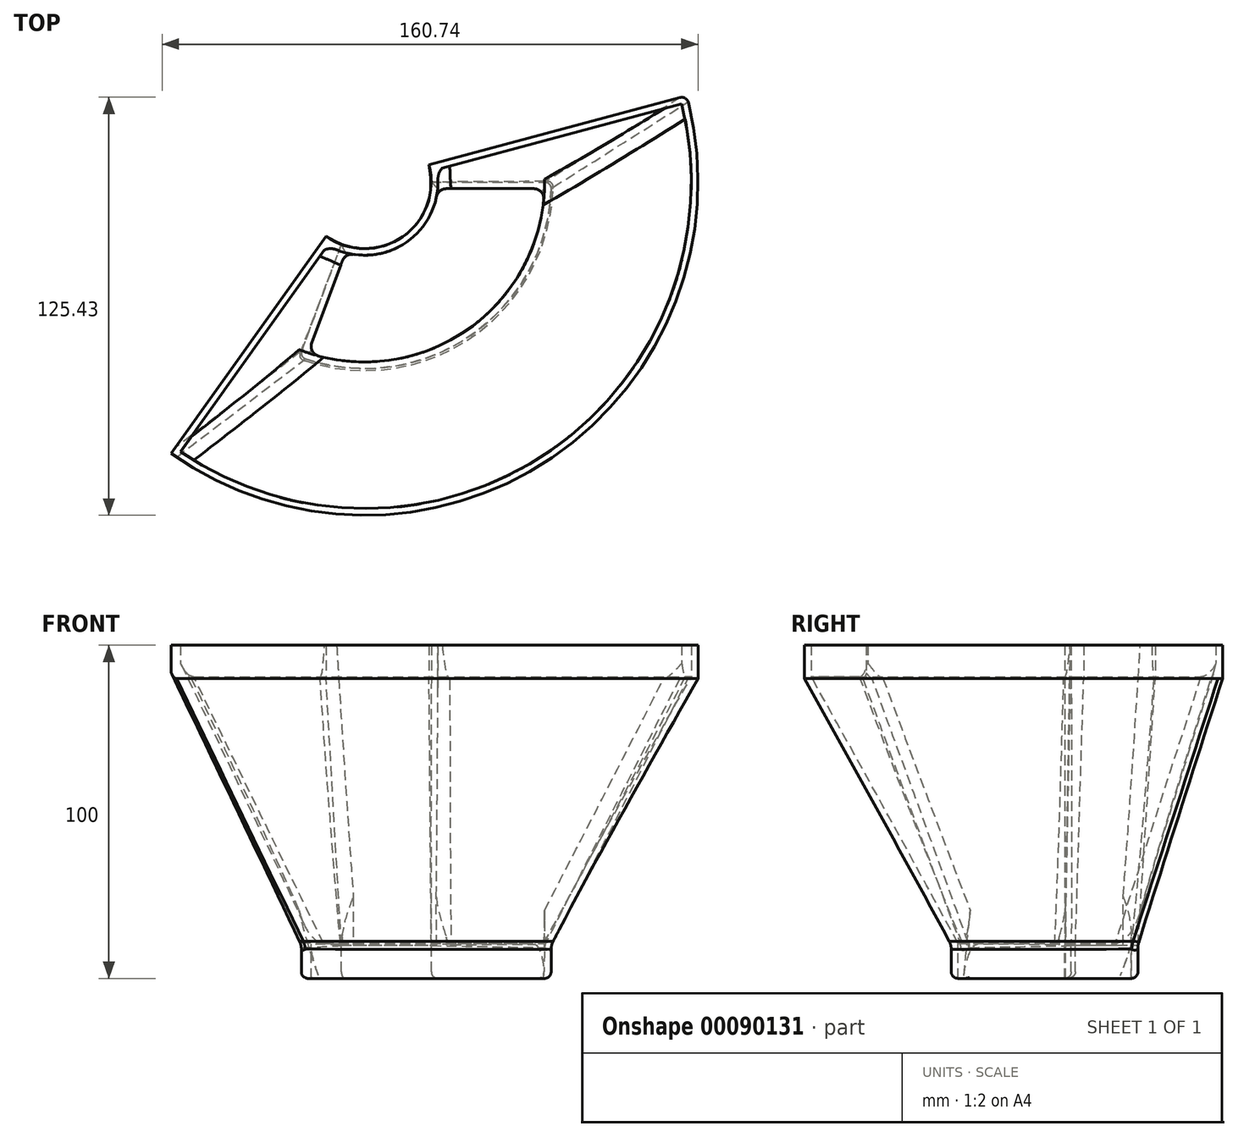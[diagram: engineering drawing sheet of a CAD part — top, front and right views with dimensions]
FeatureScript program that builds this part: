
annotation { "Feature Type Name" : "Feature", "Feature Type Description" : "" }
export const myFeature = defineFeature(function(context is Context, id is Id, definition is map)
    precondition{}
    {
        {
            var Q0;
            Q0=qCreatedBy(makeId("Top.planeOp"),FACE);
            var sketch = newSketch(context, id + "F0", { "sketchPlane" : qUnion([Q0])});
            skArc(sketch, "E0", {"start": v(-6.99, -18.74) * mm, "mid": v(11.4, -16.43) * mm, "end": v(20, 0) * mm});
            skArc(sketch, "E1", {"start": v(56, 0) * mm, "mid": v(31.94, -46) * mm, "end": v(-19.57, -52.47) * mm});
            skLineSegment(sketch, "E2", {"start": v(-6.99, -18.74) * mm, "end": v(-19.57, -52.47) * mm});
            skLineSegment(sketch, "E3", {"start": v(-19.57, -52.47) * mm, "end": v(56, 0) * mm, "construction": true});
            skLineSegment(sketch, "E4", {"start": v(20, 0) * mm, "end": v(56, 0) * mm});
            skLineSegment(sketch, "E5", {"start": v(-19.57, -52.47) * mm, "end": v(0, 0) * mm, "construction": true});
            skLineSegment(sketch, "E6", {"start": v(0, 0) * mm, "end": v(56, 0) * mm, "construction": true});
            skSolve(sketch);
        }
        {
            var Q0;
            Q0=makeQuery(id+"F0.imprint","IMPRINT",FACE,{"disambiguationData":[TD([[makeQuery(id+"F0.imprint","IMPRINT",EDGE,{"derivedFrom":sQuery(id+"F0.wireOp",EDGE,"E0")}),-1.0]])]});
            cPlane(context, id + "F1", {"entities" : qUnion([Q0]), "cplaneType" : CPlaneType.OFFSET, "offset" : 80 * mm, "width" : 150 * mm, "height" : 150 * mm});
        }
        {
            var Q0;
            Q0=makeQuery(id+"F0.imprint","IMPRINT",FACE,{"disambiguationData":[TD([[makeQuery(id+"F0.imprint","IMPRINT",EDGE,{"derivedFrom":sQuery(id+"F0.wireOp",EDGE,"E0")}),-1.0]])]});
            extrude(context, id + "F2", {"entities" : qUnion([Q0]), "oppositeDirection" : true, "depth" : 10 * mm, "hasDraft" : true, "draftAngle" : 0 * degree});
        }
        {
            var Q0;
            Q0=qCreatedBy(id+"F1.planeOp",FACE);
            var sketch = newSketch(context, id + "F3", { "sketchPlane" : qUnion([Q0])});
            skArc(sketch, "E7", {"start": v(57.03, -82.14) * mm, "mid": v(93.9, -34.39) * mm, "end": v(96.6, 25.88) * mm});
            skArc(sketch, "E8", {"start": v(19.32, 5.18) * mm, "mid": v(11.4, -16.43) * mm, "end": v(-11.6, -16.3) * mm});
            skPoint(sketch, "E9.0", {"position": v(31.94, -46) * mm});
            skLineSegment(sketch, "E10", {"start": v(0, 0) * mm, "end": v(57.03, -82.14) * mm, "construction": true});
            skArc(sketch, "E11.MirrorCS", {"start": v(57.03, -82.14) * mm, "mid": v(-0.6, -100) * mm, "end": v(-58, -81.46) * mm});
            skLineSegment(sketch, "E12", {"start": v(19.32, 5.18) * mm, "end": v(96.6, 25.88) * mm});
            skLineSegment(sketch, "E13.MirrorCS", {"start": v(-11.6, -16.3) * mm, "end": v(-58, -81.46) * mm});
            skSolve(sketch);
        }
        {
            var Q0;
            Q0 = qSketchRegion(id + "F3", true);
            extrude(context, id + "F4", {"entities" : qUnion([Q0]), "depth" : 10 * mm, "hasDraft" : true, "draftAngle" : 0 * degree});
        }
        {
            var Q0;
            Q0=makeQuery(id+"F2.opExtrude","CAP_FACE",FACE,{"disambiguationData":[OSD([sQuery(id+"F0.wireOp",EDGE,"E0"),sQuery(id+"F0.wireOp",EDGE,"E1"),sQuery(id+"F0.wireOp",EDGE,"E2"),sQuery(id+"F0.wireOp",EDGE,"E4")])],"isStart":true});
            var Q1;
            Q1=makeQuery(id+"F4.opExtrude","CAP_FACE",FACE,{"disambiguationData":[OSD([sQuery(id+"F3.wireOp",EDGE,"nCj7gBB7-4aPa-FVLX-MlBj-FOoPtuo5CQov"),sQuery(id+"F3.wireOp",EDGE,"LFc6QFRy-mYMp-mxdy-AK87-V1AcJNPdvyw2"),sQuery(id+"F3.wireOp",EDGE,"E7"),sQuery(id+"F3.wireOp",EDGE,"E8")])],"isStart":true});
            loft(context, id + "F5", {"sheetProfilesArray" : [{ "sheetProfileEntities" : qUnion([Q0]) }, { "sheetProfileEntities" : qUnion([Q1]) }]});
        }
        {
            var Q0;
            Q0=makeQuery(id+"F4.opExtrude","SWEPT_BODY",BODY,{"disambiguationData":[OSD([sQuery(id+"F3.wireOp",EDGE,"nCj7gBB7-4aPa-FVLX-MlBj-FOoPtuo5CQov"),sQuery(id+"F3.wireOp",EDGE,"LFc6QFRy-mYMp-mxdy-AK87-V1AcJNPdvyw2"),sQuery(id+"F3.wireOp",EDGE,"E7"),sQuery(id+"F3.wireOp",EDGE,"E8")])]});
            var Q1;
            Q1=makeQuery(id+"F5.opLoft","SWEPT_BODY",BODY,{"disambiguationData":[OSD([sQuery(id+"F0.wireOp",EDGE,"E0"),sQuery(id+"F0.wireOp",EDGE,"E1"),sQuery(id+"F0.wireOp",EDGE,"E2"),sQuery(id+"F0.wireOp",EDGE,"E4"),sQuery(id+"F3.wireOp",EDGE,"nCj7gBB7-4aPa-FVLX-MlBj-FOoPtuo5CQov"),sQuery(id+"F3.wireOp",EDGE,"LFc6QFRy-mYMp-mxdy-AK87-V1AcJNPdvyw2"),sQuery(id+"F3.wireOp",EDGE,"E7"),sQuery(id+"F3.wireOp",EDGE,"E8")])]});
            var Q2;
            Q2=makeQuery(id+"F2.opExtrude","SWEPT_BODY",BODY,{"disambiguationData":[OSD([sQuery(id+"F0.wireOp",EDGE,"E0"),sQuery(id+"F0.wireOp",EDGE,"E1"),sQuery(id+"F0.wireOp",EDGE,"E2"),sQuery(id+"F0.wireOp",EDGE,"E4")])]});
            booleanBodies(context, id + "F6", {"operationType" : BooleanOperationType.UNION, "tools" : qUnion([Q0, Q1, Q2])});
        }
        {
            var Q0;
            Q0=makeQuery(id+"F4.opExtrude","CAP_FACE",FACE,{"disambiguationData":[OSD([sQuery(id+"F3.wireOp",EDGE,"nCj7gBB7-4aPa-FVLX-MlBj-FOoPtuo5CQov"),sQuery(id+"F3.wireOp",EDGE,"LFc6QFRy-mYMp-mxdy-AK87-V1AcJNPdvyw2"),sQuery(id+"F3.wireOp",EDGE,"E7"),sQuery(id+"F3.wireOp",EDGE,"E8")])],"isStart":false});
            var Q1;
            Q1=makeQuery(id+"F2.opExtrude","CAP_FACE",FACE,{"disambiguationData":[OSD([sQuery(id+"F0.wireOp",EDGE,"E0"),sQuery(id+"F0.wireOp",EDGE,"E1"),sQuery(id+"F0.wireOp",EDGE,"E2"),sQuery(id+"F0.wireOp",EDGE,"E4")])],"isStart":false});
            shell(context, id + "F7", {"entities" : qUnion([Q0, Q1]), "thickness" : 2 * mm});
        }
        {
            var Q0;
            Q0=makeQuery(id+"F7.opShell","OFFSET_EDGE",EDGE,{"disambiguationData":[OSD([sQuery(id+"F0.wireOp",EDGE,"E0"),sQuery(id+"F0.wireOp",EDGE,"E2"),sQuery(id+"F3.wireOp",EDGE,"E8"),sQuery(id+"F3.wireOp",EDGE,"E13.MirrorCS")])]});
            var Q1;
            Q1=makeQuery(id+"F7.opShell","OFFSET_EDGE",EDGE,{"disambiguationData":[OSD([sQuery(id+"F0.wireOp",EDGE,"E1"),sQuery(id+"F0.wireOp",EDGE,"E2"),sQuery(id+"F3.wireOp",EDGE,"E11.MirrorCS"),sQuery(id+"F3.wireOp",EDGE,"E13.MirrorCS")])]});
            var Q2;
            Q2=makeQuery(id+"F7.opShell","OFFSET_EDGE",EDGE,{"disambiguationData":[OSD([sQuery(id+"F0.wireOp",EDGE,"E1"),sQuery(id+"F0.wireOp",EDGE,"E4"),sQuery(id+"F3.wireOp",EDGE,"E7"),sQuery(id+"F3.wireOp",EDGE,"E12")])]});
            var Q3;
            Q3=makeQuery(id+"F7.opShell","OFFSET_EDGE",EDGE,{"disambiguationData":[OSD([sQuery(id+"F0.wireOp",EDGE,"E0"),sQuery(id+"F0.wireOp",EDGE,"E4"),sQuery(id+"F3.wireOp",EDGE,"E8"),sQuery(id+"F3.wireOp",EDGE,"E12")])]});
            fillet(context, id + "F8", {"entities" : qUnion([Q0, Q1, Q2, Q3]), "radius" : 4.8 * mm, "tangentPropagation" : true, "allowEdgeOverflow" : false});
        }
        {
            var Q0;
            {var subQ0=sQuery(id+"F3.wireOp",EDGE,"E8");var subQ1=sQuery(id+"F3.wireOp",EDGE,"LFc6QFRy-mYMp-mxdy-AK87-V1AcJNPdvyw2");var subQ2=sQuery(id+"F0.wireOp",EDGE,"E2");var subQ3=sQuery(id+"F0.wireOp",EDGE,"E0");Q0=makeQuery(id+"F6.opBoolean","MERGE",EDGE,{"derivedFrom":[makeQuery(id+"F2.opExtrude","SWEPT_EDGE",EDGE,{"disambiguationData":[OSD([subQ3,subQ2])]}),makeQuery(id+"F4.opExtrude","SWEPT_EDGE",EDGE,{"disambiguationData":[OSD([subQ1,subQ0])]}),makeQuery(id+"F5.opLoft","SWEPT_EDGE",EDGE,{"disambiguationData":[OSD([subQ3,subQ2,subQ1,subQ0])]})]});}
            var Q1;
            {var subQ0=sQuery(id+"F3.wireOp",EDGE,"E8");var subQ1=sQuery(id+"F3.wireOp",EDGE,"nCj7gBB7-4aPa-FVLX-MlBj-FOoPtuo5CQov");var subQ2=sQuery(id+"F0.wireOp",EDGE,"E4");var subQ3=sQuery(id+"F0.wireOp",EDGE,"E0");Q1=makeQuery(id+"F6.opBoolean","MERGE",EDGE,{"derivedFrom":[makeQuery(id+"F2.opExtrude","SWEPT_EDGE",EDGE,{"disambiguationData":[OSD([subQ3,subQ2])]}),makeQuery(id+"F4.opExtrude","SWEPT_EDGE",EDGE,{"disambiguationData":[OSD([subQ1,subQ0])]}),makeQuery(id+"F5.opLoft","SWEPT_EDGE",EDGE,{"disambiguationData":[OSD([subQ3,subQ2,subQ1,subQ0])]})]});}
            var Q2;
            Q2=makeQuery(id+"F2.opExtrude","SWEPT_EDGE",EDGE,{"disambiguationData":[OSD([sQuery(id+"F0.wireOp",EDGE,"E1"),sQuery(id+"F0.wireOp",EDGE,"E2")])]});
            var Q3;
            Q3=makeQuery(id+"F5.opLoft","SWEPT_EDGE",EDGE,{"disambiguationData":[OSD([sQuery(id+"F0.wireOp",EDGE,"E1"),sQuery(id+"F0.wireOp",EDGE,"E2"),sQuery(id+"F3.wireOp",EDGE,"LFc6QFRy-mYMp-mxdy-AK87-V1AcJNPdvyw2"),sQuery(id+"F3.wireOp",EDGE,"E7")])]});
            var Q4;
            Q4=makeQuery(id+"F4.opExtrude","SWEPT_EDGE",EDGE,{"disambiguationData":[OSD([sQuery(id+"F3.wireOp",EDGE,"LFc6QFRy-mYMp-mxdy-AK87-V1AcJNPdvyw2"),sQuery(id+"F3.wireOp",EDGE,"E7")])]});
            var Q5;
            Q5=makeQuery(id+"F4.opExtrude","SWEPT_EDGE",EDGE,{"disambiguationData":[OSD([sQuery(id+"F3.wireOp",EDGE,"nCj7gBB7-4aPa-FVLX-MlBj-FOoPtuo5CQov"),sQuery(id+"F3.wireOp",EDGE,"E7")])]});
            var Q6;
            Q6=makeQuery(id+"F5.opLoft","SWEPT_EDGE",EDGE,{"disambiguationData":[OSD([sQuery(id+"F0.wireOp",EDGE,"E1"),sQuery(id+"F0.wireOp",EDGE,"E4"),sQuery(id+"F3.wireOp",EDGE,"nCj7gBB7-4aPa-FVLX-MlBj-FOoPtuo5CQov"),sQuery(id+"F3.wireOp",EDGE,"E7")])]});
            var Q7;
            Q7=makeQuery(id+"F2.opExtrude","SWEPT_EDGE",EDGE,{"disambiguationData":[OSD([sQuery(id+"F0.wireOp",EDGE,"E1"),sQuery(id+"F0.wireOp",EDGE,"E4")])]});
            var Q8;
            Q8=makeQuery(id+"F2.opExtrude","CAP_EDGE",EDGE,{"disambiguationData":[OSD([sQuery(id+"F0.wireOp",EDGE,"E4")])],"isStart":false});
            var Q9;
            Q9=makeQuery(id+"F2.opExtrude","CAP_EDGE",EDGE,{"disambiguationData":[OSD([sQuery(id+"F0.wireOp",EDGE,"E1")])],"isStart":false});
            var Q10;
            Q10=makeQuery(id+"F2.opExtrude","CAP_EDGE",EDGE,{"disambiguationData":[OSD([sQuery(id+"F0.wireOp",EDGE,"E2")])],"isStart":false});
            var Q11;
            Q11=makeQuery(id+"F2.opExtrude","CAP_EDGE",EDGE,{"disambiguationData":[OSD([sQuery(id+"F0.wireOp",EDGE,"E0")])],"isStart":false});
            fillet(context, id + "F9", {"entities" : qUnion([Q0, Q1, Q2, Q3, Q4, Q5, Q6, Q7, Q8, Q9, Q10, Q11]), "radius" : 2 * mm, "tangentPropagation" : true, "allowEdgeOverflow" : false});
        }
        {
            var Q0;
            {var subQ0=sQuery(id+"F3.wireOp",EDGE,"E8");var subQ1=sQuery(id+"F3.wireOp",EDGE,"nCj7gBB7-4aPa-FVLX-MlBj-FOoPtuo5CQov");var subQ2=sQuery(id+"F0.wireOp",EDGE,"E4");var subQ3=sQuery(id+"F0.wireOp",EDGE,"E0");Q0=makeQuery(id+"F9.opFillet","BLEND_EDGE",EDGE,{"blendedFrom":[makeQuery(id+"F6.opBoolean","MERGE",EDGE,{"derivedFrom":[makeQuery(id+"F2.opExtrude","SWEPT_EDGE",EDGE,{"disambiguationData":[OSD([subQ3,subQ2])]}),makeQuery(id+"F4.opExtrude","SWEPT_EDGE",EDGE,{"disambiguationData":[OSD([subQ1,subQ0])]}),makeQuery(id+"F5.opLoft","SWEPT_EDGE",EDGE,{"disambiguationData":[OSD([subQ3,subQ2,subQ1,subQ0])]})]}),makeQuery(id+"F6.opBoolean","MERGE",FACE,{"derivedFrom":[makeQuery(id+"F2.opExtrude","SWEPT_FACE",FACE,{"disambiguationData":[OSD([subQ2])]}),makeQuery(id+"F4.opExtrude","SWEPT_FACE",FACE,{"disambiguationData":[OSD([subQ1])]}),makeQuery(id+"F5.opLoft","SWEPT_FACE",FACE,{"disambiguationData":[OSD([subQ3,sQuery(id+"F0.wireOp",EDGE,"E1"),subQ2,subQ1,sQuery(id+"F3.wireOp",EDGE,"E7"),subQ0])]})]})],"blendedInto":[makeQuery(id+"F6.opBoolean","MERGE",FACE,{"derivedFrom":[makeQuery(id+"F2.opExtrude","SWEPT_FACE",FACE,{"disambiguationData":[OSD([subQ2])]}),makeQuery(id+"F4.opExtrude","SWEPT_FACE",FACE,{"disambiguationData":[OSD([subQ1])]}),makeQuery(id+"F5.opLoft","SWEPT_FACE",FACE,{"disambiguationData":[OSD([subQ3,sQuery(id+"F0.wireOp",EDGE,"E1"),subQ2,subQ1,sQuery(id+"F3.wireOp",EDGE,"E7"),subQ0])]})]})]});}
            var Q1;
            {var subQ0=sQuery(id+"F0.wireOp",EDGE,"E1");Q1=makeQuery(id+"F6.opBoolean","MERGE",EDGE,{"derivedFrom":[makeQuery(id+"F2.opExtrude","CAP_EDGE",EDGE,{"disambiguationData":[OSD([subQ0])],"isStart":true}),makeQuery(id+"F5.opLoft","MID_CAP_EDGE",EDGE,{"disambiguationData":[OSD([subQ0,sQuery(id+"F0.wireOp",EDGE,"E2"),sQuery(id+"F0.wireOp",EDGE,"E4")])],"capPos":0.0})]});}
            fillet(context, id + "F10", {"entities" : qUnion([Q0, Q1]), "radius" : 5 * mm, "tangentPropagation" : true, "allowEdgeOverflow" : false});
        }
        {
            var Q0;
            Q0=makeQuery(id+"F7.opShell","OFFSET_EDGE",EDGE,{"disambiguationData":[OSD([sQuery(id+"F0.wireOp",EDGE,"E1"),sQuery(id+"F0.wireOp",EDGE,"E2")])]});
            var Q1;
            Q1=makeQuery(id+"F7.opShell","OFFSET_EDGE",EDGE,{"disambiguationData":[OSD([sQuery(id+"F0.wireOp",EDGE,"E1"),sQuery(id+"F0.wireOp",EDGE,"E4")])]});
            var Q2;
            Q2=makeQuery(id+"F7.opShell","OFFSET_EDGE",EDGE,{"disambiguationData":[OSD([sQuery(id+"F0.wireOp",EDGE,"E0"),sQuery(id+"F0.wireOp",EDGE,"E2")])]});
            var Q3;
            Q3=makeQuery(id+"F7.opShell","OFFSET_EDGE",EDGE,{"disambiguationData":[OSD([sQuery(id+"F0.wireOp",EDGE,"E0"),sQuery(id+"F0.wireOp",EDGE,"E4")])]});
            fillet(context, id + "F11", {"entities" : qUnion([Q0, Q1, Q2, Q3]), "radius" : 3 * mm, "tangentPropagation" : true, "allowEdgeOverflow" : false});
        }
    });
